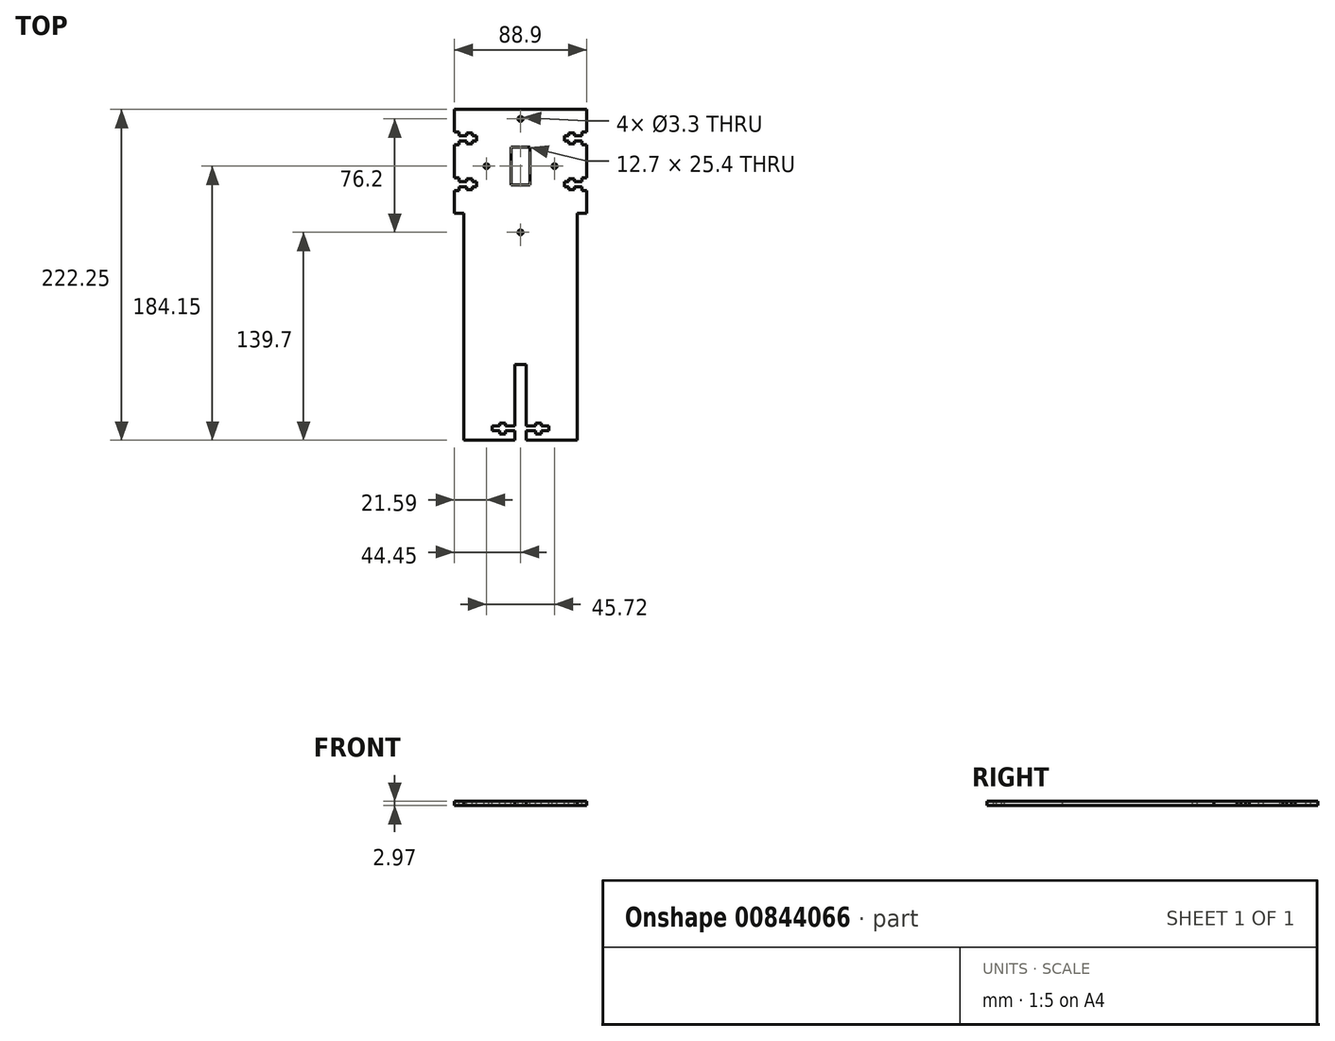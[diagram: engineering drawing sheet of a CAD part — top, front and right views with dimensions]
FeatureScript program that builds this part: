
annotation { "Feature Type Name" : "Feature", "Feature Type Description" : "" }
export const myFeature = defineFeature(function(context is Context, id is Id, definition is map)
    precondition{}
    {
        {
            var Q0;
            Q0=qCreatedBy(makeId("Top.planeOp"),FACE);
            var sketch = newSketch(context, id + "F0", { "sketchPlane" : qUnion([Q0])});
            skLineSegment(sketch, "E0", {"start": v(0, 0) * mm, "end": v(0, 152.4) * mm});
            skLineSegment(sketch, "E1", {"start": v(0, 222.25) * mm, "end": v(76.2, 222.25) * mm});
            skLineSegment(sketch, "E2", {"start": v(76.2, 152.4) * mm, "end": v(76.2, 0) * mm});
            skLineSegment(sketch, "E3", {"start": v(76.2, 0) * mm, "end": v(0, 0) * mm});
            skLineSegment(sketch, "E4", {"start": v(0, 222.25) * mm, "end": v(-6.35, 222.25) * mm});
            skLineSegment(sketch, "E5", {"start": v(76.2, 222.25) * mm, "end": v(82.55, 222.25) * mm});
            skLineSegment(sketch, "E6", {"start": v(82.55, 222.25) * mm, "end": v(82.55, 152.4) * mm});
            skLineSegment(sketch, "E7", {"start": v(82.55, 152.4) * mm, "end": v(76.2, 152.4) * mm});
            skLineSegment(sketch, "E8", {"start": v(-6.35, 222.25) * mm, "end": v(-6.35, 152.4) * mm});
            skLineSegment(sketch, "E9", {"start": v(-6.35, 152.4) * mm, "end": v(0, 152.4) * mm});
            skSolve(sketch);
        }
        {
            var Q0;
            Q0 = qSketchRegion(id + "F0", true);
            extrude(context, id + "F1", {"entities" : qUnion([Q0]), "depth" : 2.97 * mm, "offsetDistance" : 25.4 * mm});
        }
        {
            var Q0;
            Q0=makeQuery(id+"F1.opExtrude","CAP_FACE",FACE,{"disambiguationData":[OSD([sQuery(id+"F0.wireOp",EDGE,"E0"),sQuery(id+"F0.wireOp",EDGE,"E1"),sQuery(id+"F0.wireOp",EDGE,"E2"),sQuery(id+"F0.wireOp",EDGE,"E3"),sQuery(id+"F0.wireOp",EDGE,"E4"),sQuery(id+"F0.wireOp",EDGE,"E5"),sQuery(id+"F0.wireOp",EDGE,"E6"),sQuery(id+"F0.wireOp",EDGE,"E7"),sQuery(id+"F0.wireOp",EDGE,"E8"),sQuery(id+"F0.wireOp",EDGE,"E9")])],"isStart":false});
            var sketch = newSketch(context, id + "F2", { "sketchPlane" : qUnion([Q0])});
            skCircle(sketch, "E10", {"center": v(38.1, 215.9) * mm, "radius": 1.65 * mm});
            skCircle(sketch, "E11", {"center": v(60.96, 184.15) * mm, "radius": 1.65 * mm});
            skCircle(sketch, "E12", {"center": v(15.24, 184.15) * mm, "radius": 1.65 * mm});
            skLineSegment(sketch, "E13.bottom", {"start": v(31.75, 196.85) * mm, "end": v(44.45, 196.85) * mm});
            skLineSegment(sketch, "E13.top", {"start": v(31.75, 171.45) * mm, "end": v(44.45, 171.45) * mm});
            skLineSegment(sketch, "E13.left", {"start": v(31.75, 196.85) * mm, "end": v(31.75, 171.45) * mm});
            skLineSegment(sketch, "E13.right", {"start": v(44.45, 196.85) * mm, "end": v(44.45, 171.45) * mm});
            skLineSegment(sketch, "E14.bottom", {"start": v(34.3, 0) * mm, "end": v(41.91, 0) * mm});
            skLineSegment(sketch, "E14.top", {"start": v(34.3, 50.8) * mm, "end": v(41.91, 50.8) * mm});
            skLineSegment(sketch, "E14.left", {"start": v(34.3, 0) * mm, "end": v(34.3, 6.35) * mm});
            skLineSegment(sketch, "E14.right", {"start": v(41.91, 0) * mm, "end": v(41.91, 6.35) * mm});
            skLineSegment(sketch, "E15.bottom", {"start": v(41.91, 9.65) * mm, "end": v(48.26, 9.65) * mm});
            skLineSegment(sketch, "E15.top", {"start": v(41.91, 6.35) * mm, "end": v(48.26, 6.35) * mm});
            skLineSegment(sketch, "E16", {"start": v(48.26, 6.35) * mm, "end": v(48.26, 4.32) * mm});
            skLineSegment(sketch, "E17", {"start": v(48.26, 4.32) * mm, "end": v(52.07, 4.32) * mm});
            skLineSegment(sketch, "E18", {"start": v(52.07, 4.32) * mm, "end": v(52.07, 6.35) * mm});
            skLineSegment(sketch, "E19", {"start": v(52.07, 11.68) * mm, "end": v(48.26, 11.68) * mm});
            skLineSegment(sketch, "E20", {"start": v(48.26, 11.68) * mm, "end": v(48.26, 9.65) * mm});
            skLineSegment(sketch, "E21.bottom", {"start": v(34.3, 9.65) * mm, "end": v(27.94, 9.65) * mm});
            skLineSegment(sketch, "E21.top", {"start": v(34.3, 6.35) * mm, "end": v(27.94, 6.35) * mm});
            skLineSegment(sketch, "E22", {"start": v(27.94, 9.65) * mm, "end": v(27.94, 11.68) * mm});
            skLineSegment(sketch, "E23", {"start": v(27.94, 6.35) * mm, "end": v(27.94, 4.32) * mm});
            skLineSegment(sketch, "E24", {"start": v(27.94, 4.32) * mm, "end": v(24.13, 4.32) * mm});
            skLineSegment(sketch, "E25", {"start": v(24.13, 4.32) * mm, "end": v(24.13, 6.35) * mm});
            skLineSegment(sketch, "E26", {"start": v(24.13, 11.68) * mm, "end": v(27.94, 11.68) * mm});
            skLineSegment(sketch, "E27", {"start": v(27.94, 11.68) * mm, "end": v(27.94, 11.68) * mm});
            skLineSegment(sketch, "E28.trimOffspring", {"start": v(34.3, 9.65) * mm, "end": v(34.3, 50.8) * mm});
            skLineSegment(sketch, "E29.trimOffspring", {"start": v(41.91, 9.65) * mm, "end": v(41.91, 50.8) * mm});
            skCircle(sketch, "E30", {"center": v(101.6, 63.5) * mm, "radius": 1.65 * mm});
            skLineSegment(sketch, "E31.bottom", {"start": v(24.13, 9.65) * mm, "end": v(19.05, 9.65) * mm});
            skLineSegment(sketch, "E31.top", {"start": v(24.13, 6.35) * mm, "end": v(19.05, 6.35) * mm});
            skLineSegment(sketch, "E31.right", {"start": v(19.05, 9.65) * mm, "end": v(19.05, 6.35) * mm});
            skLineSegment(sketch, "E32.bottom", {"start": v(52.07, 9.65) * mm, "end": v(57.15, 9.65) * mm});
            skLineSegment(sketch, "E32.top", {"start": v(52.07, 6.35) * mm, "end": v(57.15, 6.35) * mm});
            skLineSegment(sketch, "E32.right", {"start": v(57.15, 9.65) * mm, "end": v(57.15, 6.35) * mm});
            skLineSegment(sketch, "E33.trimOffspring", {"start": v(52.07, 9.65) * mm, "end": v(52.07, 11.68) * mm});
            skLineSegment(sketch, "E34.trimOffspring", {"start": v(24.13, 9.65) * mm, "end": v(24.13, 11.68) * mm});
            skLineSegment(sketch, "E35.bottom", {"start": v(-6.35, 176.28) * mm, "end": v(-3.3, 176.28) * mm});
            skLineSegment(sketch, "E35.top", {"start": v(-6.35, 167.9) * mm, "end": v(-3.3, 167.9) * mm});
            skLineSegment(sketch, "E35.left", {"start": v(-6.35, 176.28) * mm, "end": v(-6.35, 167.9) * mm});
            skLineSegment(sketch, "E35.right", {"start": v(-3.3, 176.28) * mm, "end": v(-3.3, 173.74) * mm});
            skLineSegment(sketch, "E36.bottom", {"start": v(-3.3, 173.74) * mm, "end": v(1.78, 173.74) * mm});
            skLineSegment(sketch, "E36.top", {"start": v(-3.3, 170.43) * mm, "end": v(1.78, 170.43) * mm});
            skLineSegment(sketch, "E37.bottom", {"start": v(1.78, 168.4) * mm, "end": v(5.59, 168.4) * mm});
            skLineSegment(sketch, "E37.top", {"start": v(1.78, 175.77) * mm, "end": v(5.59, 175.77) * mm});
            skLineSegment(sketch, "E37.left", {"start": v(1.78, 168.4) * mm, "end": v(1.78, 170.43) * mm});
            skLineSegment(sketch, "E37.right", {"start": v(5.59, 168.4) * mm, "end": v(5.59, 170.43) * mm});
            skLineSegment(sketch, "E38.bottom", {"start": v(5.59, 173.74) * mm, "end": v(8.64, 173.74) * mm});
            skLineSegment(sketch, "E38.top", {"start": v(5.59, 170.43) * mm, "end": v(8.64, 170.43) * mm});
            skLineSegment(sketch, "E38.right", {"start": v(8.64, 173.74) * mm, "end": v(8.64, 170.43) * mm});
            skLineSegment(sketch, "E39.bottom", {"start": v(-6.35, 207) * mm, "end": v(-3.3, 207) * mm});
            skLineSegment(sketch, "E39.top", {"start": v(-6.35, 198.63) * mm, "end": v(-3.3, 198.63) * mm});
            skLineSegment(sketch, "E39.left", {"start": v(-6.35, 207) * mm, "end": v(-6.35, 198.63) * mm});
            skLineSegment(sketch, "E39.right", {"start": v(-3.3, 207) * mm, "end": v(-3.3, 204.47) * mm});
            skLineSegment(sketch, "E40.bottom", {"start": v(-3.3, 204.47) * mm, "end": v(1.78, 204.47) * mm});
            skLineSegment(sketch, "E40.top", {"start": v(-3.3, 201.17) * mm, "end": v(1.78, 201.17) * mm});
            skLineSegment(sketch, "E41.bottom", {"start": v(1.78, 199.14) * mm, "end": v(5.59, 199.14) * mm});
            skLineSegment(sketch, "E41.top", {"start": v(1.78, 206.5) * mm, "end": v(5.59, 206.5) * mm});
            skLineSegment(sketch, "E41.left", {"start": v(1.78, 199.14) * mm, "end": v(1.78, 201.17) * mm});
            skLineSegment(sketch, "E41.right", {"start": v(5.59, 199.14) * mm, "end": v(5.59, 201.17) * mm});
            skLineSegment(sketch, "E42.bottom", {"start": v(5.59, 204.47) * mm, "end": v(8.64, 204.47) * mm});
            skLineSegment(sketch, "E42.top", {"start": v(5.59, 201.17) * mm, "end": v(8.64, 201.17) * mm});
            skLineSegment(sketch, "E42.right", {"start": v(8.64, 204.47) * mm, "end": v(8.64, 201.17) * mm});
            skLineSegment(sketch, "E43.trimOffspring", {"start": v(-3.3, 201.17) * mm, "end": v(-3.3, 198.63) * mm});
            skLineSegment(sketch, "E44.trimOffspring", {"start": v(1.78, 204.47) * mm, "end": v(1.78, 206.5) * mm});
            skLineSegment(sketch, "E45.trimOffspring", {"start": v(5.59, 204.47) * mm, "end": v(5.59, 206.5) * mm});
            skLineSegment(sketch, "E46.trimOffspring", {"start": v(5.59, 173.74) * mm, "end": v(5.59, 175.77) * mm});
            skLineSegment(sketch, "E47.trimOffspring", {"start": v(1.78, 173.74) * mm, "end": v(1.78, 175.77) * mm});
            skLineSegment(sketch, "E48.trimOffspring", {"start": v(-3.3, 170.43) * mm, "end": v(-3.3, 167.9) * mm});
            skLineSegment(sketch, "E49.bottom", {"start": v(82.55, 198.63) * mm, "end": v(79.5, 198.63) * mm});
            skLineSegment(sketch, "E49.top", {"start": v(82.55, 207) * mm, "end": v(79.5, 207) * mm});
            skLineSegment(sketch, "E49.left", {"start": v(82.55, 198.63) * mm, "end": v(82.55, 207) * mm});
            skLineSegment(sketch, "E49.right", {"start": v(79.5, 198.63) * mm, "end": v(79.5, 201.17) * mm});
            skLineSegment(sketch, "E50.bottom", {"start": v(79.5, 201.17) * mm, "end": v(74.42, 201.17) * mm});
            skLineSegment(sketch, "E50.top", {"start": v(79.5, 204.47) * mm, "end": v(74.42, 204.47) * mm});
            skLineSegment(sketch, "E51.bottom", {"start": v(74.42, 206.5) * mm, "end": v(70.61, 206.5) * mm});
            skLineSegment(sketch, "E51.top", {"start": v(74.42, 199.14) * mm, "end": v(70.61, 199.14) * mm});
            skLineSegment(sketch, "E51.left", {"start": v(74.42, 206.5) * mm, "end": v(74.42, 204.47) * mm});
            skLineSegment(sketch, "E51.right", {"start": v(70.61, 206.5) * mm, "end": v(70.61, 204.47) * mm});
            skLineSegment(sketch, "E52.bottom", {"start": v(70.61, 201.17) * mm, "end": v(67.56, 201.17) * mm});
            skLineSegment(sketch, "E52.top", {"start": v(70.61, 204.47) * mm, "end": v(67.56, 204.47) * mm});
            skLineSegment(sketch, "E52.right", {"start": v(67.56, 201.17) * mm, "end": v(67.56, 204.47) * mm});
            skLineSegment(sketch, "E53.bottom", {"start": v(82.55, 167.9) * mm, "end": v(79.5, 167.9) * mm});
            skLineSegment(sketch, "E53.top", {"start": v(82.55, 176.28) * mm, "end": v(79.5, 176.28) * mm});
            skLineSegment(sketch, "E53.left", {"start": v(82.55, 167.9) * mm, "end": v(82.55, 176.28) * mm});
            skLineSegment(sketch, "E53.right", {"start": v(79.5, 167.9) * mm, "end": v(79.5, 170.43) * mm});
            skLineSegment(sketch, "E54.bottom", {"start": v(79.5, 170.43) * mm, "end": v(74.42, 170.43) * mm});
            skLineSegment(sketch, "E54.top", {"start": v(79.5, 173.74) * mm, "end": v(74.42, 173.74) * mm});
            skLineSegment(sketch, "E55.bottom", {"start": v(74.42, 175.77) * mm, "end": v(70.61, 175.77) * mm});
            skLineSegment(sketch, "E55.top", {"start": v(74.42, 168.4) * mm, "end": v(70.61, 168.4) * mm});
            skLineSegment(sketch, "E55.left", {"start": v(74.42, 175.77) * mm, "end": v(74.42, 173.74) * mm});
            skLineSegment(sketch, "E55.right", {"start": v(70.61, 175.77) * mm, "end": v(70.61, 173.74) * mm});
            skLineSegment(sketch, "E56.bottom", {"start": v(70.61, 170.43) * mm, "end": v(67.56, 170.43) * mm});
            skLineSegment(sketch, "E56.top", {"start": v(70.61, 173.74) * mm, "end": v(67.56, 173.74) * mm});
            skLineSegment(sketch, "E56.right", {"start": v(67.56, 170.43) * mm, "end": v(67.56, 173.74) * mm});
            skLineSegment(sketch, "E57.trimOffspring", {"start": v(79.5, 173.74) * mm, "end": v(79.5, 176.28) * mm});
            skLineSegment(sketch, "E58.trimOffspring", {"start": v(74.42, 170.43) * mm, "end": v(74.42, 168.4) * mm});
            skLineSegment(sketch, "E59.trimOffspring", {"start": v(70.61, 170.43) * mm, "end": v(70.61, 168.4) * mm});
            skLineSegment(sketch, "E60.trimOffspring", {"start": v(70.61, 201.17) * mm, "end": v(70.61, 199.14) * mm});
            skLineSegment(sketch, "E61.trimOffspring", {"start": v(74.42, 201.17) * mm, "end": v(74.42, 199.14) * mm});
            skLineSegment(sketch, "E62.trimOffspring", {"start": v(79.5, 204.47) * mm, "end": v(79.5, 207) * mm});
            skCircle(sketch, "E63", {"center": v(38.1, 139.7) * mm, "radius": 1.65 * mm});
            skSolve(sketch);
        }
        {
            var Q0;
            Q0 = qSketchRegion(id + "F2", true);
            extrude(context, id + "F3", {"entities" : qUnion([Q0]), "operationType" : NewBodyOperationType.REMOVE, "endBound" : BoundingType.THROUGH_ALL, "oppositeDirection" : true, "depth" : 25.4 * mm, "offsetDistance" : 25.4 * mm});
        }
    });
